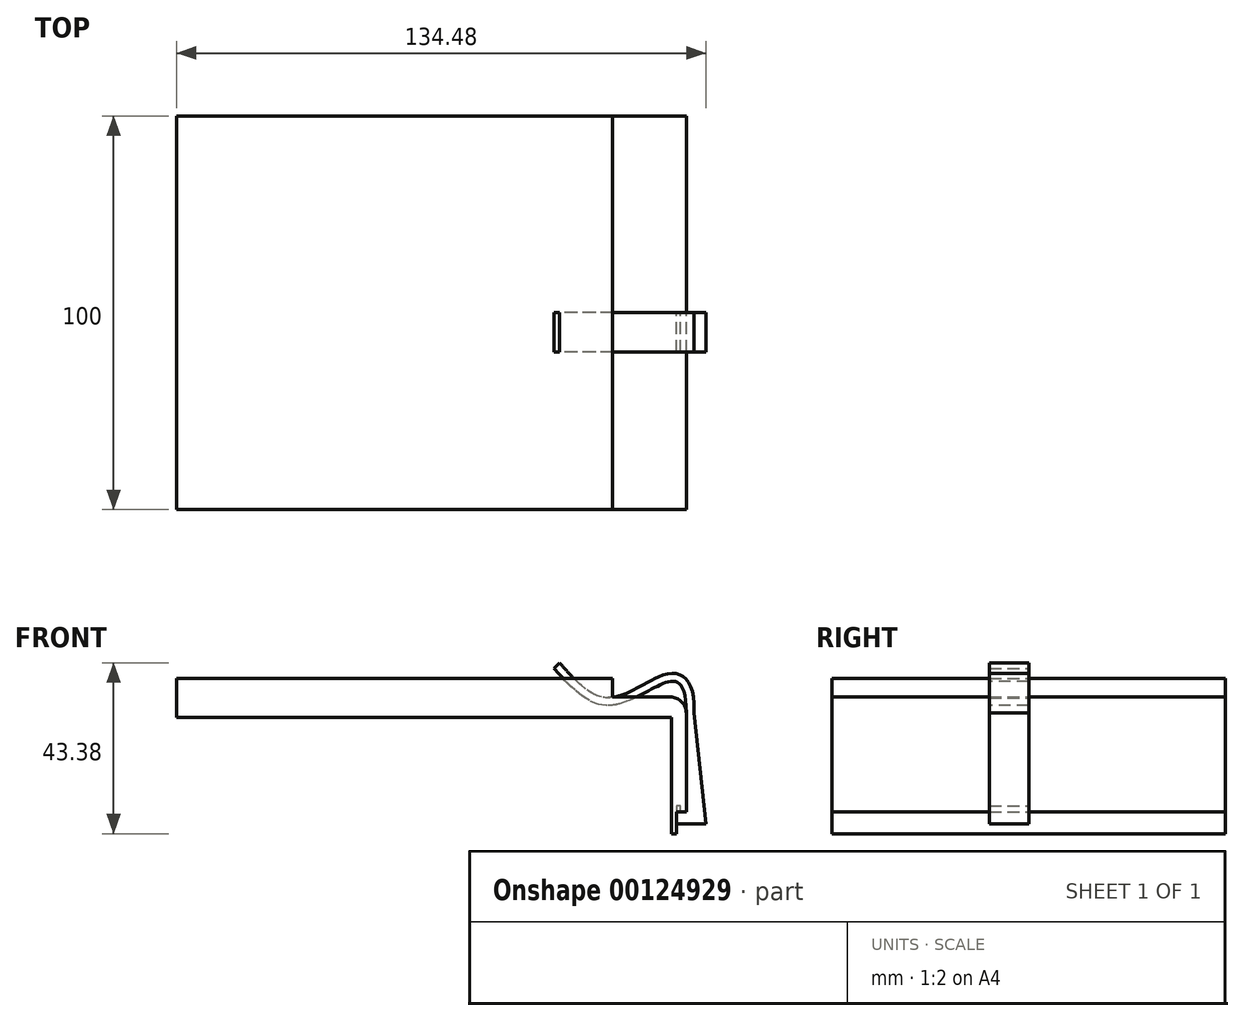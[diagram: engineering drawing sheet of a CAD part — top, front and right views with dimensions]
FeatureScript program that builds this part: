
annotation { "Feature Type Name" : "Feature", "Feature Type Description" : "" }
export const myFeature = defineFeature(function(context is Context, id is Id, definition is map)
    precondition{}
    {
        {
            var Q0;
            Q0=qCreatedBy(makeId("Front.planeOp"),FACE);
            var sketch = newSketch(context, id + "F0", { "sketchPlane" : qUnion([Q0])});
            skLineSegment(sketch, "E0", {"start": v(0, 34.7) * mm, "end": v(-18.75, 34.7) * mm});
            skLineSegment(sketch, "E1", {"start": v(-18.75, 34.7) * mm, "end": v(-18.75, 39.5) * mm});
            skLineSegment(sketch, "E2", {"start": v(-18.75, 39.5) * mm, "end": v(-129.48, 39.5) * mm});
            skLineSegment(sketch, "E3", {"start": v(-129.48, 39.5) * mm, "end": v(-129.48, 29.5) * mm});
            skLineSegment(sketch, "E4", {"start": v(-3.8, 0) * mm, "end": v(-2.5, 0) * mm});
            skLineSegment(sketch, "E5", {"start": v(-2.5, 0) * mm, "end": v(-2.5, 5.5) * mm});
            skLineSegment(sketch, "E6", {"start": v(-2.5, 5.5) * mm, "end": v(0, 5.5) * mm});
            skLineSegment(sketch, "E7", {"start": v(0, 5.5) * mm, "end": v(0, 34.7) * mm});
            skLineSegment(sketch, "E8", {"start": v(-3.8, 0) * mm, "end": v(-3.8, 29.5) * mm});
            skLineSegment(sketch, "E9", {"start": v(-3.8, 29.5) * mm, "end": v(-129.48, 29.5) * mm});
            skPoint(sketch, "E10.orphan", {"position": v(0, 0) * mm});
            skSolve(sketch);
        }
        {
            var Q0;
            Q0=makeQuery(id+"F0.imprint","IMPRINT",FACE,{"disambiguationData":[TD([[makeQuery(id+"F0.imprint","IMPRINT",EDGE,{"derivedFrom":sQuery(id+"F0.wireOp",EDGE,"E0")}),1.0]])]});
            extrude(context, id + "F1", {"entities" : qUnion([Q0]), "endBound" : BoundingType.SYMMETRIC, "depth" : 100 * mm});
        }
        {
            var Q0;
            Q0=makeQuery(id+"F1.opExtrude","SWEPT_EDGE",EDGE,{"disambiguationData":[OSD([sQuery(id+"F0.wireOp",EDGE,"E0"),sQuery(id+"F0.wireOp",EDGE,"E7")])]});
            fillet(context, id + "F2", {"entities" : qUnion([Q0]), "radius" : 4 * mm, "tangentPropagation" : true, "allowEdgeOverflow" : false});
        }
        {
            var Q0;
            Q0=qCreatedBy(makeId("Front.planeOp"),FACE);
            var sketch = newSketch(context, id + "F3", { "sketchPlane" : qUnion([Q0])});
            skLineSegment(sketch, "E11.2", {"start": v(0, 5.5) * mm, "end": v(0, 30.7) * mm});
            skLineSegment(sketch, "E11.3", {"start": v(-1.5, 5.5) * mm, "end": v(0, 5.5) * mm});
            skLineSegment(sketch, "E12", {"start": v(5, 33.57) * mm, "end": v(5, 0) * mm});
            skLineSegment(sketch, "E13", {"start": v(-2.5, 5.5) * mm, "end": v(-2.5, 2.5) * mm});
            skLineSegment(sketch, "E14", {"start": v(-2.5, 2.5) * mm, "end": v(5, 2.5) * mm});
            skLineSegment(sketch, "E15", {"start": v(-1.5, 5.5) * mm, "end": v(-1.5, 7) * mm});
            skLineSegment(sketch, "E16", {"start": v(-1.5, 7) * mm, "end": v(-2.5, 7) * mm});
            skLineSegment(sketch, "E17", {"start": v(-2.5, 7) * mm, "end": v(-2.5, 5.5) * mm});
            skFitSpline(sketch, "E18", {"points": [v(0, 30.7) * mm, v(-6.86, 37.7) * mm, v(-22.23, 32.8) * mm, v(-33.63, 42) * mm], "startDerivative": vector(0, 97.53) * mm, "endDerivative": vector(-13.92, 14.47) * mm});
            skFitSpline(sketch, "E19.0", {"points": [v(2, 30.7) * mm, v(2, 31.77) * mm, v(1.92, 33.68) * mm, v(1.56, 36) * mm, v(1.03, 37.58) * mm, v(0.42, 38.66) * mm, v(-0.16, 39.38) * mm, v(-0.86, 39.97) * mm, v(-1.66, 40.4) * mm, v(-2.5, 40.64) * mm, v(-3.58, 40.76) * mm, v(-4.84, 40.6) * mm, v(-6.23, 40.17) * mm, v(-7.32, 39.7) * mm, v(-8.18, 39.3) * mm, v(-9.03, 38.88) * mm, v(-10.1, 38.32) * mm, v(-11.8, 37.4) * mm, v(-13.91, 36.29) * mm, v(-16.4, 35.2) * mm, v(-18.35, 34.66) * mm, v(-19.82, 34.52) * mm, v(-20.7, 34.55) * mm, v(-21.38, 34.66) * mm, v(-21.88, 34.78) * mm, v(-22.4, 34.95) * mm, v(-23.13, 35.25) * mm, v(-24.05, 35.73) * mm, v(-25.18, 36.48) * mm, v(-26.3, 37.34) * mm, v(-27.74, 38.6) * mm, v(-29.07, 39.94) * mm, v(-30.22, 41.2) * mm, v(-30.99, 42.05) * mm, v(-31.64, 42.8) * mm, v(-32, 43.2) * mm, v(-32.18, 43.38) * mm]});
            skLineSegment(sketch, "E20", {"start": v(2, 30.7) * mm, "end": v(5, 2.5) * mm});
            skLineSegment(sketch, "E21", {"start": v(-32.18, 43.38) * mm, "end": v(-33.63, 42) * mm});
            skSolve(sketch);
        }
        {
            var Q0;
            Q0 = qSketchRegion(id + "F3", true);
            extrude(context, id + "F4", {"entities" : qUnion([Q0]), "depth" : 10 * mm});
        }
    });
